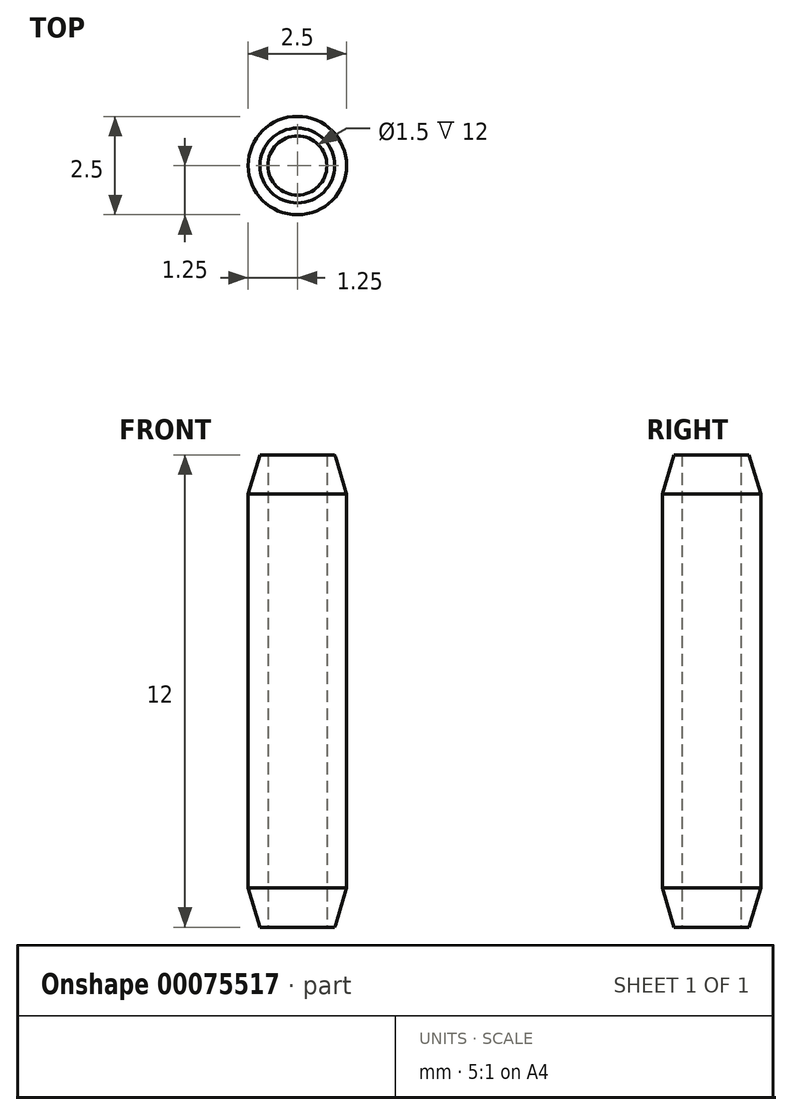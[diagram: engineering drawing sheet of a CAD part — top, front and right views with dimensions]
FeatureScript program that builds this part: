
annotation { "Feature Type Name" : "Feature", "Feature Type Description" : "" }
export const myFeature = defineFeature(function(context is Context, id is Id, definition is map)
    precondition{}
    {
        {
            var Q0;
            Q0=qCreatedBy(makeId("Top.planeOp"),FACE);
            var sketch = newSketch(context, id + "F0", { "sketchPlane" : qUnion([Q0])});
            skCircle(sketch, "E0", {"center": v(0, 0) * mm, "radius": 1.25 * mm});
            skSolve(sketch);
        }
        {
            var Q0;
            Q0 = qSketchRegion(id + "F0", true);
            extrude(context, id + "F1", {"entities" : qUnion([Q0]), "endBound" : BoundingType.SYMMETRIC, "depth" : 12 * mm});
        }
        {
            var Q0;
            Q0=makeQuery(id+"F1.opExtrude","CAP_FACE",FACE,{"disambiguationData":[OSD([sQuery(id+"F0.wireOp",EDGE,"E0")])],"isStart":true});
            var sketch = newSketch(context, id + "F2", { "sketchPlane" : qUnion([Q0])});
            skCircle(sketch, "E1", {"center": v(0, 0) * mm, "radius": 0.75 * mm});
            skSolve(sketch);
        }
        {
            var Q0;
            Q0 = qSketchRegion(id + "F2", true);
            extrude(context, id + "F3", {"entities" : qUnion([Q0]), "operationType" : NewBodyOperationType.REMOVE, "endBound" : BoundingType.UP_TO_NEXT, "oppositeDirection" : true, "depth" : 25 * mm});
        }
        {
            var Q0;
            Q0=makeQuery(id+"F1.opExtrude","CAP_EDGE",EDGE,{"disambiguationData":[OSD([sQuery(id+"F0.wireOp",EDGE,"E0")])],"isStart":true});
            var Q1;
            Q1=makeQuery(id+"F1.opExtrude","CAP_EDGE",EDGE,{"disambiguationData":[OSD([sQuery(id+"F0.wireOp",EDGE,"E0")])],"isStart":false});
            chamfer(context, id + "F4", {"entities" : qUnion([Q0, Q1]), "chamferType" : ChamferType.TWO_OFFSETS, "width1" : 1 * mm, "oppositeDirection" : false, "width2" : 0.3 * mm, "tangentPropagation" : true});
        }
    });
